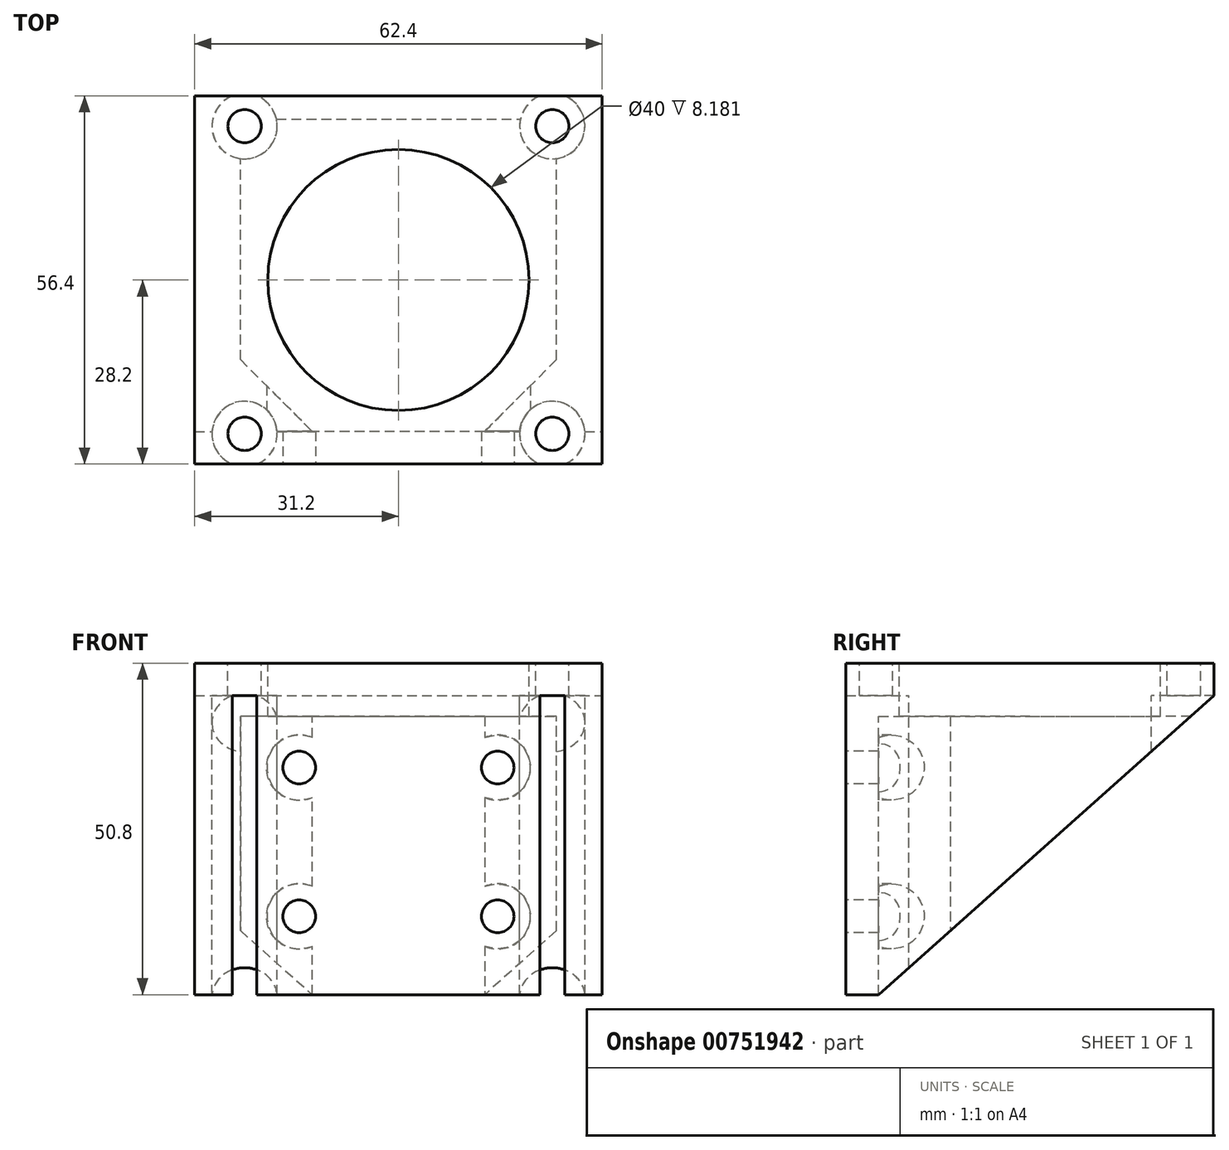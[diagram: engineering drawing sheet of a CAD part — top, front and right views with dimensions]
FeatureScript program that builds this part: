
annotation { "Feature Type Name" : "Feature", "Feature Type Description" : "" }
export const myFeature = defineFeature(function(context is Context, id is Id, definition is map)
    precondition{}
    {
        {
            var Q0;
            Q0=qCreatedBy(makeId("Top.planeOp"),FACE);
            var sketch = newSketch(context, id + "F0", { "sketchPlane" : qUnion([Q0])});
            skLineSegment(sketch, "E0.bottom", {"start": v(-31.2, 28.2) * mm, "end": v(31.2, 28.2) * mm});
            skLineSegment(sketch, "E0.top", {"start": v(-31.2, -28.2) * mm, "end": v(31.2, -28.2) * mm});
            skLineSegment(sketch, "E0.left", {"start": v(-31.2, 28.2) * mm, "end": v(-31.2, -28.2) * mm});
            skLineSegment(sketch, "E0.right", {"start": v(31.2, 28.2) * mm, "end": v(31.2, -28.2) * mm});
            skPoint(sketch, "E0.middle", {"position": v(0, 0) * mm});
            skSolve(sketch);
        }
        {
            var Q0;
            Q0 = qSketchRegion(id + "F0", true);
            extrude(context, id + "F1", {"entities" : qUnion([Q0]), "oppositeDirection" : true, "depth" : 50.8 * mm, "offsetDistance" : 25.4 * mm});
        }
        {
            var Q0;
            Q0=makeQuery(id+"F1.opExtrude","SWEPT_FACE",FACE,{"disambiguationData":[OSD([sQuery(id+"F0.wireOp",EDGE,"E0.right")])]});
            var sketch = newSketch(context, id + "F2", { "sketchPlane" : qUnion([Q0])});
            skLineSegment(sketch, "E1", {"start": v(28.2, -5) * mm, "end": v(-23.2, -50.8) * mm});
            skLineSegment(sketch, "E2", {"start": v(-23.2, -50.8) * mm, "end": v(-28.2, -50.8) * mm});
            skLineSegment(sketch, "E3", {"start": v(-28.2, -50.8) * mm, "end": v(-28.2, -53.7) * mm});
            skLineSegment(sketch, "E4", {"start": v(-28.2, -53.7) * mm, "end": v(30.05, -53.7) * mm});
            skLineSegment(sketch, "E5", {"start": v(30.05, -53.7) * mm, "end": v(30.05, -5) * mm});
            skLineSegment(sketch, "E6", {"start": v(30.05, -5) * mm, "end": v(28.2, -5) * mm});
            skSolve(sketch);
        }
        {
            var Q0;
            Q0 = qSketchRegion(id + "F2", true);
            extrude(context, id + "F3", {"entities" : qUnion([Q0]), "operationType" : NewBodyOperationType.REMOVE, "endBound" : BoundingType.THROUGH_ALL, "oppositeDirection" : true, "depth" : 25.4 * mm, "offsetDistance" : 25.4 * mm});
        }
        {
            var Q0;
            Q0=qCreatedBy(makeId("Front.planeOp"),FACE);
            cPlane(context, id + "F4", {"entities" : qUnion([Q0]), "cplaneType" : CPlaneType.OFFSET, "offset" : 25.4 * mm, "oppositeDirection" : true, "width" : 152.4 * mm, "height" : 152.4 * mm});
        }
        {
            var Q0;
            Q0=qCreatedBy(id+"F4.planeOp",FACE);
            var sketch = newSketch(context, id + "F5", { "sketchPlane" : qUnion([Q0])});
            skLineSegment(sketch, "E7.bottom", {"start": v(24.2, -8.18) * mm, "end": v(-24.2, -8.18) * mm});
            skLineSegment(sketch, "E7.top", {"start": v(24.2, -50.8) * mm, "end": v(-24.2, -50.8) * mm});
            skLineSegment(sketch, "E7.left", {"start": v(24.2, -8.18) * mm, "end": v(24.2, -50.8) * mm});
            skLineSegment(sketch, "E7.right", {"start": v(-24.2, -8.18) * mm, "end": v(-24.2, -50.8) * mm});
            skPoint(sketch, "E7.middle", {"position": v(0, -29.5) * mm});
            skSolve(sketch);
        }
        {
            var Q0;
            Q0 = qSketchRegion(id + "F5", true);
            var Q1;
            Q1=makeQuery(id+"F3.boolean.opBoolean","COPY",VERTEX,{"derivedFrom":makeQuery(id+"F3.opExtrude","CAP_VERTEX",VERTEX,{"disambiguationData":[OSD([sQuery(id+"F0.wireOp",EDGE,"E0.right"),sQuery(id+"F2.wireOp",EDGE,"E1"),sQuery(id+"F2.wireOp",EDGE,"E2")])],"isStart":true})});
            extrude(context, id + "F6", {"entities" : qUnion([Q0]), "operationType" : NewBodyOperationType.REMOVE, "endBound" : BoundingType.UP_TO_VERTEX, "depth" : 50.55 * mm, "endBoundEntityVertex" : qUnion([Q1]), "offsetDistance" : 25.4 * mm});
        }
        {
            var Q0;
            Q0=makeQuery(id+"F6.boolean.opBoolean","COPY",EDGE,{"derivedFrom":makeQuery(id+"F6.opExtrude","CAP_EDGE",EDGE,{"disambiguationData":[OSD([sQuery(id+"F5.wireOp",EDGE,"E7.left")])],"isStart":false})});
            var Q1;
            Q1=makeQuery(id+"F6.boolean.opBoolean","COPY",EDGE,{"derivedFrom":makeQuery(id+"F6.opExtrude","CAP_EDGE",EDGE,{"disambiguationData":[OSD([sQuery(id+"F5.wireOp",EDGE,"E7.right")])],"isStart":false})});
            chamfer(context, id + "F7", {"entities" : qUnion([Q0, Q1]), "width" : 11 * mm, "tangentPropagation" : true});
        }
        {
            var Q0;
            Q0=qCreatedBy(makeId("Top.planeOp"),FACE);
            var sketch = newSketch(context, id + "F8", { "sketchPlane" : qUnion([Q0])});
            skCircle(sketch, "E8", {"center": v(0, 0) * mm, "radius": 20 * mm});
            skLineSegment(sketch, "E9.bottom", {"start": v(-23.57, 23.57) * mm, "end": v(23.57, 23.57) * mm, "construction": true});
            skLineSegment(sketch, "E9.top", {"start": v(-23.57, -23.57) * mm, "end": v(23.57, -23.57) * mm, "construction": true});
            skLineSegment(sketch, "E9.left", {"start": v(-23.57, 23.57) * mm, "end": v(-23.57, -23.57) * mm, "construction": true});
            skLineSegment(sketch, "E9.right", {"start": v(23.57, 23.57) * mm, "end": v(23.57, -23.57) * mm, "construction": true});
            skCircle(sketch, "E10", {"center": v(-23.57, 23.57) * mm, "radius": 2.55 * mm});
            skCircle(sketch, "E11", {"center": v(23.57, 23.57) * mm, "radius": 2.55 * mm});
            skCircle(sketch, "E12", {"center": v(23.57, -23.57) * mm, "radius": 2.55 * mm});
            skCircle(sketch, "E13", {"center": v(-23.57, -23.57) * mm, "radius": 2.55 * mm});
            skSolve(sketch);
        }
        {
            var Q0;
            Q0 = qSketchRegion(id + "F8", true);
            extrude(context, id + "F9", {"entities" : qUnion([Q0]), "operationType" : NewBodyOperationType.REMOVE, "endBound" : BoundingType.THROUGH_ALL, "oppositeDirection" : true, "depth" : 25.4 * mm, "offsetDistance" : 25.4 * mm});
        }
        {
            var Q0;
            Q0=qCreatedBy(makeId("Top.planeOp"),FACE);
            cPlane(context, id + "F10", {"entities" : qUnion([Q0]), "cplaneType" : CPlaneType.OFFSET, "offset" : 5 * mm, "oppositeDirection" : true, "width" : 152.4 * mm, "height" : 152.4 * mm});
        }
        {
            var Q0;
            Q0=qCreatedBy(id+"F10.planeOp",FACE);
            var sketch = newSketch(context, id + "F11", { "sketchPlane" : qUnion([Q0])});
            skCircle(sketch, "E14.0", {"center": v(23.57, -23.57) * mm, "radius": 2.55 * mm, "construction": true});
            skLineSegment(sketch, "E15.bottom", {"start": v(23.57, -23.57) * mm, "end": v(-23.57, -23.57) * mm, "construction": true});
            skLineSegment(sketch, "E15.top", {"start": v(23.57, 23.57) * mm, "end": v(-23.57, 23.57) * mm, "construction": true});
            skLineSegment(sketch, "E15.left", {"start": v(23.57, -23.57) * mm, "end": v(23.57, 23.57) * mm, "construction": true});
            skLineSegment(sketch, "E15.right", {"start": v(-23.57, -23.57) * mm, "end": v(-23.57, 23.57) * mm, "construction": true});
            skPoint(sketch, "E15.middle", {"position": v(0, 0) * mm});
            skCircle(sketch, "E16", {"center": v(-23.57, -23.57) * mm, "radius": 5 * mm});
            skCircle(sketch, "E17", {"center": v(23.57, -23.57) * mm, "radius": 5 * mm});
            skCircle(sketch, "E18", {"center": v(-23.57, 23.57) * mm, "radius": 5 * mm});
            skCircle(sketch, "E19", {"center": v(23.57, 23.57) * mm, "radius": 5 * mm});
            skSolve(sketch);
        }
        {
            var Q0;
            Q0 = qSketchRegion(id + "F11", true);
            extrude(context, id + "F12", {"entities" : qUnion([Q0]), "operationType" : NewBodyOperationType.REMOVE, "endBound" : BoundingType.THROUGH_ALL, "oppositeDirection" : true, "depth" : 25.4 * mm, "offsetDistance" : 25.4 * mm});
        }
        {
            var Q0;
            Q0=makeQuery(id+"F1.opExtrude","SWEPT_FACE",FACE,{"disambiguationData":[OSD([sQuery(id+"F0.wireOp",EDGE,"E0.top")])]});
            var sketch = newSketch(context, id + "F13", { "sketchPlane" : qUnion([Q0])});
            skLineSegment(sketch, "E20.bottom", {"start": v(15.2, -16) * mm, "end": v(-15.2, -16) * mm, "construction": true});
            skLineSegment(sketch, "E20.top", {"start": v(15.2, -38.8) * mm, "end": v(-15.2, -38.8) * mm, "construction": true});
            skLineSegment(sketch, "E20.left", {"start": v(15.2, -16) * mm, "end": v(15.2, -38.8) * mm, "construction": true});
            skLineSegment(sketch, "E20.right", {"start": v(-15.2, -16) * mm, "end": v(-15.2, -38.8) * mm, "construction": true});
            skPoint(sketch, "E20.middle", {"position": v(0, -27.4) * mm});
            skCircle(sketch, "E21", {"center": v(-15.2, -16) * mm, "radius": 2.5 * mm});
            skCircle(sketch, "E22", {"center": v(15.2, -16) * mm, "radius": 2.5 * mm});
            skCircle(sketch, "E23", {"center": v(15.2, -38.8) * mm, "radius": 2.5 * mm});
            skCircle(sketch, "E24", {"center": v(-15.2, -38.8) * mm, "radius": 2.5 * mm});
            skLineSegment(sketch, "E25", {"start": v(0, 0) * mm, "end": v(0, -27.4) * mm, "construction": true});
            skSolve(sketch);
        }
        {
            var Q0;
            Q0 = qSketchRegion(id + "F13", true);
            extrude(context, id + "F14", {"entities" : qUnion([Q0]), "operationType" : NewBodyOperationType.REMOVE, "endBound" : BoundingType.THROUGH_ALL, "oppositeDirection" : true, "depth" : 25.4 * mm, "offsetDistance" : 25.4 * mm});
        }
        {
            var Q0;
            Q0=makeQuery(id+"F1.opExtrude","SWEPT_FACE",FACE,{"disambiguationData":[OSD([sQuery(id+"F0.wireOp",EDGE,"E0.top")])]});
            var sketch = newSketch(context, id + "F15", { "sketchPlane" : qUnion([Q0])});
            skCircle(sketch, "E26", {"center": v(15.2, -38.8) * mm, "radius": 5 * mm});
            skCircle(sketch, "E27", {"center": v(-15.2, -38.8) * mm, "radius": 5 * mm});
            skCircle(sketch, "E28", {"center": v(-15.2, -16) * mm, "radius": 5 * mm});
            skCircle(sketch, "E29", {"center": v(15.2, -16) * mm, "radius": 5 * mm});
            skSolve(sketch);
        }
        {
            var Q0;
            Q0 = qSketchRegion(id + "F15", true);
            extrude(context, id + "F16", {"entities" : qUnion([Q0]), "operationType" : NewBodyOperationType.REMOVE, "oppositeDirection" : true, "depth" : 25.4 * mm, "offsetDistance" : 25.4 * mm, "hasSecondDirection" : true, "secondDirectionOppositeDirection" : true, "secondDirectionDepth" : 5 * mm});
        }
    });
